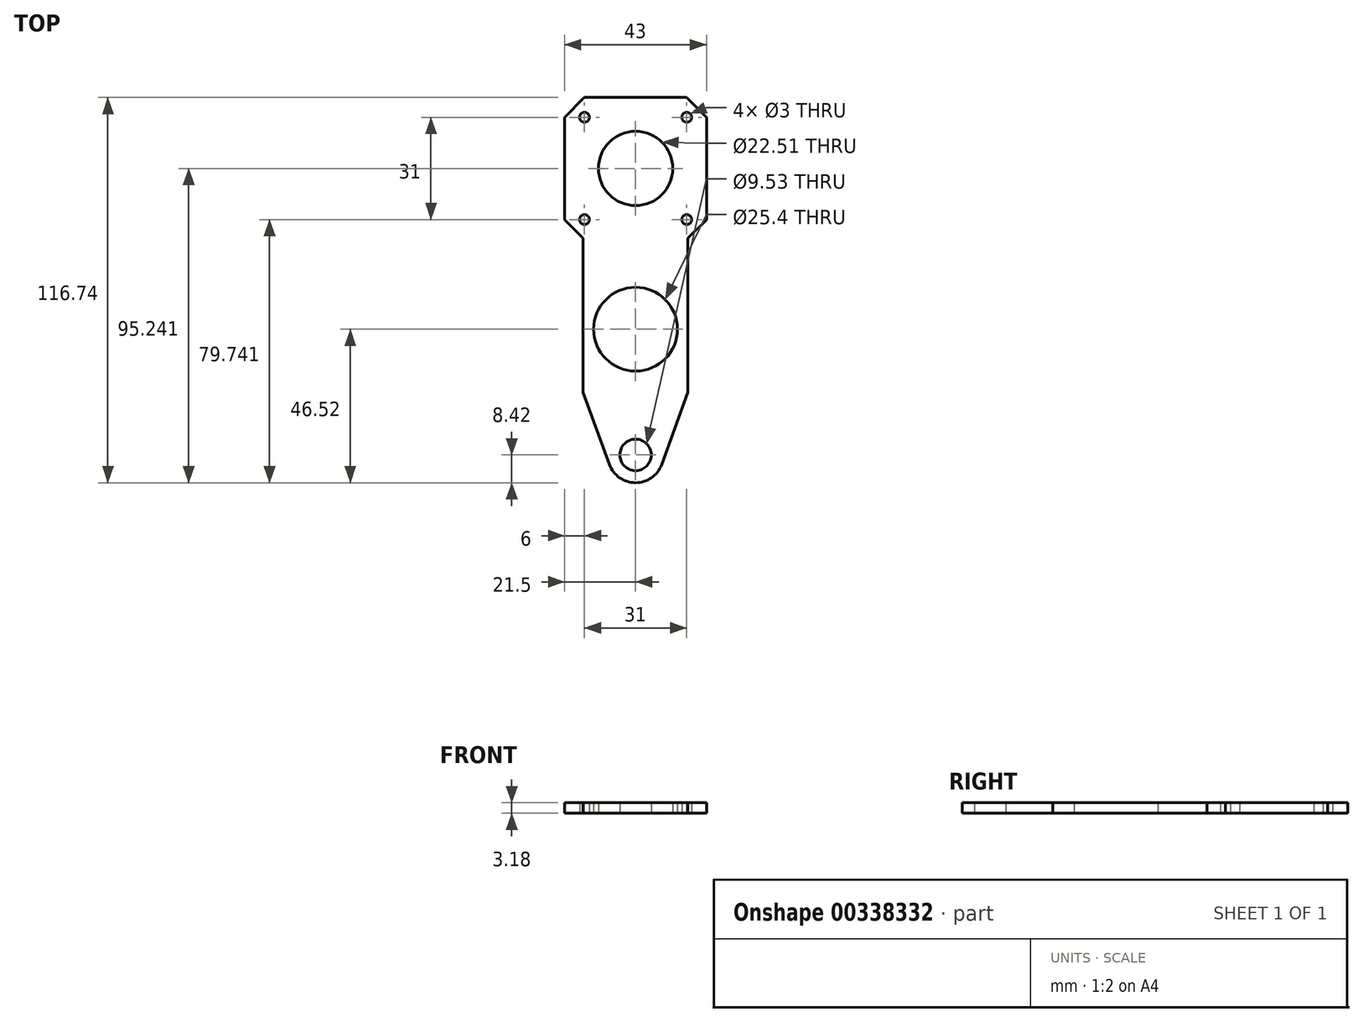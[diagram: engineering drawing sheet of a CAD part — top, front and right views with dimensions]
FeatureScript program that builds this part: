
annotation { "Feature Type Name" : "Feature", "Feature Type Description" : "" }
export const myFeature = defineFeature(function(context is Context, id is Id, definition is map)
    precondition{}
    {
        {
            var Q0;
            Q0=qCreatedBy(makeId("Top.planeOp"),FACE);
            var sketch = newSketch(context, id + "F0", { "sketchPlane" : qUnion([Q0])});
            skCircle(sketch, "E0", {"center": v(0, 0) * mm, "radius": 12.7 * mm});
            skLineSegment(sketch, "E1", {"start": v(0, 0) * mm, "end": v(0, -38.1) * mm, "construction": true});
            skCircle(sketch, "E2", {"center": v(0, -38.1) * mm, "radius": 4.76 * mm});
            skLineSegment(sketch, "E3", {"start": v(-15.88, 0) * mm, "end": v(15.87, 0) * mm});
            skLineSegment(sketch, "E4", {"start": v(0, 0) * mm, "end": v(0, 48.72) * mm, "construction": true});
            skCircle(sketch, "E5", {"center": v(0, 48.72) * mm, "radius": 11.25 * mm});
            skLineSegment(sketch, "E6.bottom", {"start": v(15.5, 33.22) * mm, "end": v(-15.5, 33.22) * mm, "construction": true});
            skLineSegment(sketch, "E6.top", {"start": v(15.5, 64.22) * mm, "end": v(-15.5, 64.22) * mm, "construction": true});
            skLineSegment(sketch, "E6.left", {"start": v(15.5, 33.22) * mm, "end": v(15.5, 64.22) * mm, "construction": true});
            skLineSegment(sketch, "E6.right", {"start": v(-15.5, 33.22) * mm, "end": v(-15.5, 64.22) * mm, "construction": true});
            skCircle(sketch, "E7", {"center": v(15.5, 33.22) * mm, "radius": 1.5 * mm});
            skCircle(sketch, "E8", {"center": v(15.5, 64.22) * mm, "radius": 1.5 * mm});
            skCircle(sketch, "E9", {"center": v(-15.5, 64.22) * mm, "radius": 1.5 * mm});
            skCircle(sketch, "E10", {"center": v(-15.5, 33.22) * mm, "radius": 1.5 * mm});
            skLineSegment(sketch, "E11", {"start": v(0, 48.72) * mm, "end": v(0, 70.22) * mm, "construction": true});
            skLineSegment(sketch, "E12", {"start": v(-21.5, 70.22) * mm, "end": v(21.5, 70.22) * mm});
            skLineSegment(sketch, "E13", {"start": v(21.5, 70.22) * mm, "end": v(21.5, 27.22) * mm});
            skLineSegment(sketch, "E14", {"start": v(21.5, 27.22) * mm, "end": v(15.88, 27.22) * mm});
            skLineSegment(sketch, "E15", {"start": v(15.87, 27.22) * mm, "end": v(15.88, -19.1) * mm});
            skLineSegment(sketch, "E16", {"start": v(15.88, -19.1) * mm, "end": v(7.91, -40.98) * mm});
            skLineSegment(sketch, "E17", {"start": v(-21.5, 70.22) * mm, "end": v(-21.5, 27.22) * mm});
            skLineSegment(sketch, "E18", {"start": v(-21.5, 27.22) * mm, "end": v(-15.87, 27.22) * mm});
            skLineSegment(sketch, "E19", {"start": v(-15.88, 27.22) * mm, "end": v(-15.88, -19.1) * mm});
            skLineSegment(sketch, "E20", {"start": v(-15.88, -19.1) * mm, "end": v(-7.91, -40.98) * mm});
            skArc(sketch, "E21", {"start": v(-7.91, -40.98) * mm, "mid": v(0, -46.52) * mm, "end": v(7.91, -40.98) * mm});
            skSolve(sketch);
        }
        {
            var Q0;
            Q0 = qSketchRegion(id + "F0", true);
            extrude(context, id + "F1", {"entities" : qUnion([Q0]), "depth" : 3.17 * mm});
        }
        {
            var Q0;
            Q0=makeQuery(id+"F1.opExtrude","SWEPT_EDGE",EDGE,{"disambiguationData":[OSD([sQuery(id+"F0.wireOp",EDGE,"E13"),sQuery(id+"F0.wireOp",EDGE,"E14")])]});
            var Q1;
            Q1=makeQuery(id+"F1.opExtrude","SWEPT_EDGE",EDGE,{"disambiguationData":[OSD([sQuery(id+"F0.wireOp",EDGE,"E12"),sQuery(id+"F0.wireOp",EDGE,"E13")])]});
            var Q2;
            Q2=makeQuery(id+"F1.opExtrude","SWEPT_EDGE",EDGE,{"disambiguationData":[OSD([sQuery(id+"F0.wireOp",EDGE,"E12"),sQuery(id+"F0.wireOp",EDGE,"E17")])]});
            var Q3;
            Q3=makeQuery(id+"F1.opExtrude","SWEPT_EDGE",EDGE,{"disambiguationData":[OSD([sQuery(id+"F0.wireOp",EDGE,"E17"),sQuery(id+"F0.wireOp",EDGE,"E18")])]});
            chamfer(context, id + "F2", {"entities" : qUnion([Q0, Q1, Q2, Q3]), "width" : 6 * mm, "tangentPropagation" : true});
        }
    });
